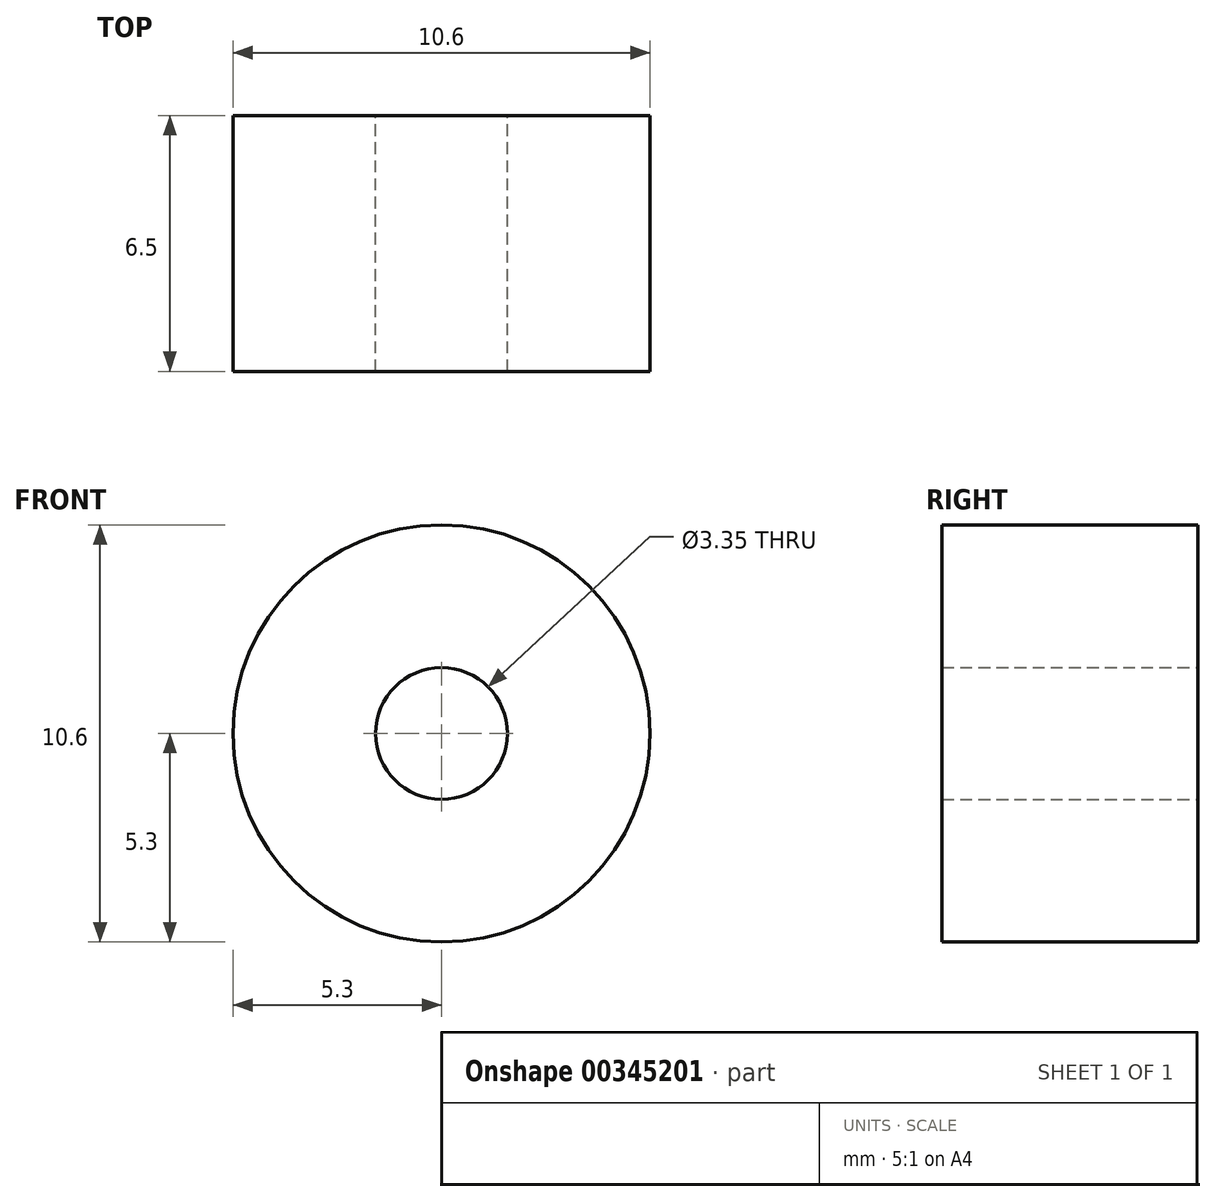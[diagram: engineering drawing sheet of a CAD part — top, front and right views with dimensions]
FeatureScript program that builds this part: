
annotation { "Feature Type Name" : "Feature", "Feature Type Description" : "" }
export const myFeature = defineFeature(function(context is Context, id is Id, definition is map)
    precondition{}
    {
        {
            var Q0;
            Q0=qCreatedBy(makeId("Front.planeOp"),FACE);
            var sketch = newSketch(context, id + "F0", { "sketchPlane" : qUnion([Q0])});
            skCircle(sketch, "E0", {"center": v(0, 0) * mm, "radius": 1.68 * mm});
            skCircle(sketch, "E1", {"center": v(0, 0) * mm, "radius": 5.3 * mm});
            skSolve(sketch);
        }
        {
            var Q0;
            Q0=makeQuery(id+"F0.imprint","IMPRINT",FACE,{"disambiguationData":[TD([[makeQuery(id+"F0.imprint","IMPRINT",EDGE,{"derivedFrom":sQuery(id+"F0.wireOp",EDGE,"E0")}),-1.0]])]});
            extrude(context, id + "F1", {"entities" : qUnion([Q0]), "depth" : 6.5 * mm});
        }
    });
